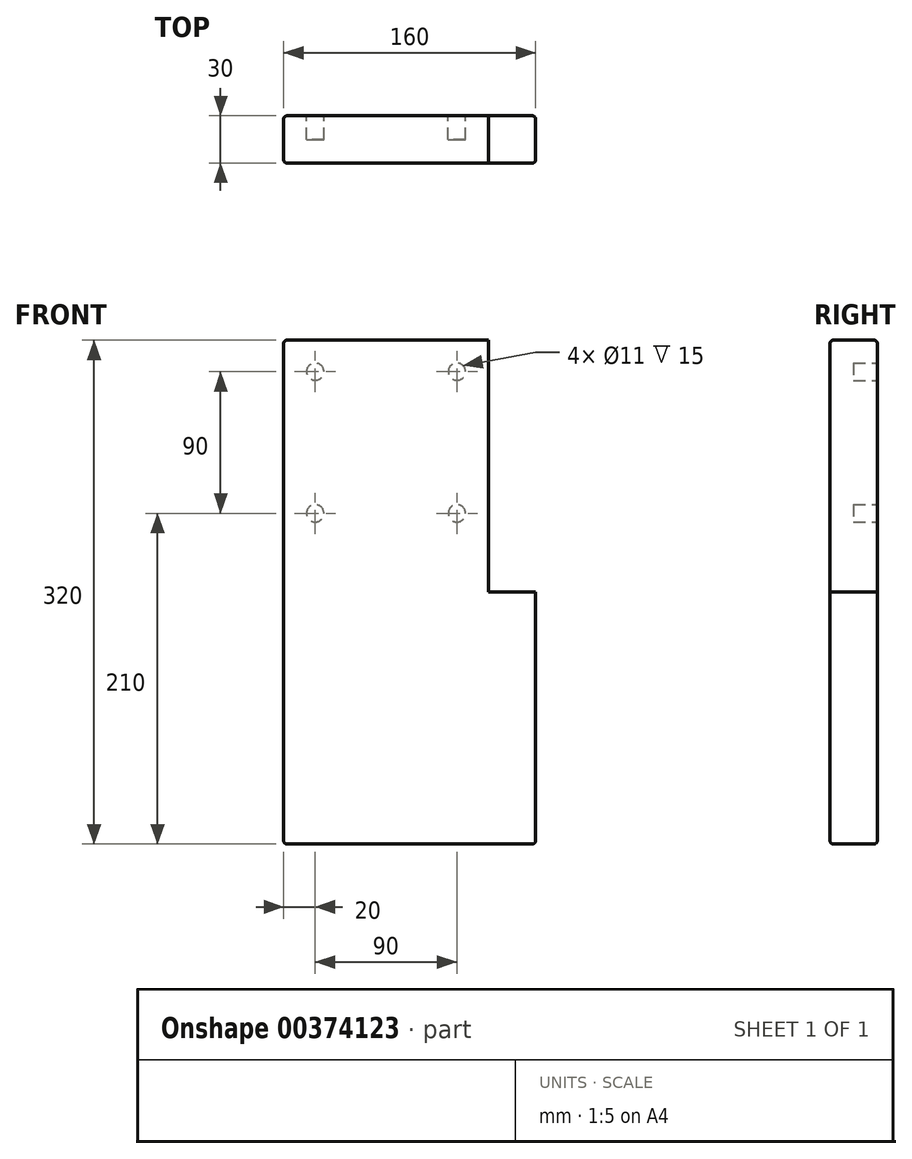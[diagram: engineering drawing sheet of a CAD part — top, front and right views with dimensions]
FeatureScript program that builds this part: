
annotation { "Feature Type Name" : "Feature", "Feature Type Description" : "" }
export const myFeature = defineFeature(function(context is Context, id is Id, definition is map)
    precondition{}
    {
        {
            var Q0;
            Q0=qCreatedBy(makeId("Top.planeOp"),FACE);
            var sketch = newSketch(context, id + "F0", { "sketchPlane" : qUnion([Q0])});
            skLineSegment(sketch, "E0.bottom", {"start": v(80, -15) * mm, "end": v(-80, -15) * mm});
            skLineSegment(sketch, "E0.top", {"start": v(80, 15) * mm, "end": v(-80, 15) * mm});
            skLineSegment(sketch, "E0.left", {"start": v(80, -15) * mm, "end": v(80, 15) * mm});
            skLineSegment(sketch, "E0.right", {"start": v(-80, -15) * mm, "end": v(-80, 15) * mm});
            skPoint(sketch, "E0.middle", {"position": v(0, 0) * mm});
            skSolve(sketch);
        }
        {
            var Q0;
            Q0 = qSketchRegion(id + "F0", true);
            extrude(context, id + "F1", {"entities" : qUnion([Q0]), "depth" : 320 * mm, "symmetric" : true});
        }
        {
            var Q0;
            Q0=makeQuery(id+"F1.opExtrude","SWEPT_FACE",FACE,{"disambiguationData":[OSD([sQuery(id+"F0.wireOp",EDGE,"E0.bottom")])]});
            var Q1;
            Q1=makeQuery(id+"F1.opExtrude","SWEPT_FACE",FACE,{"disambiguationData":[OSD([sQuery(id+"F0.wireOp",EDGE,"E0.top")])]});
            var Q2;
            Q2=makeQuery(id+"F1.opExtrude","CAP_FACE",FACE,{"disambiguationData":[OSD([sQuery(id+"F0.wireOp",EDGE,"E0.bottom"),sQuery(id+"F0.wireOp",EDGE,"E0.top"),sQuery(id+"F0.wireOp",EDGE,"E0.left"),sQuery(id+"F0.wireOp",EDGE,"E0.right")])],"isStart":false});
            var Q3;
            Q3=makeQuery(id+"F1.opExtrude","SWEPT_FACE",FACE,{"disambiguationData":[OSD([sQuery(id+"F0.wireOp",EDGE,"E0.left")])]});
            var Q4;
            Q4=makeQuery(id+"F1.opExtrude","SWEPT_FACE",FACE,{"disambiguationData":[OSD([sQuery(id+"F0.wireOp",EDGE,"E0.right")])]});
            var Q5;
            Q5=makeQuery(id+"F1.opExtrude","CAP_FACE",FACE,{"disambiguationData":[OSD([sQuery(id+"F0.wireOp",EDGE,"E0.bottom"),sQuery(id+"F0.wireOp",EDGE,"E0.top"),sQuery(id+"F0.wireOp",EDGE,"E0.left"),sQuery(id+"F0.wireOp",EDGE,"E0.right")])],"isStart":true});
            fillet(context, id + "F2", {"entities" : qUnion([Q0, Q1, Q2, Q3, Q4, Q5]), "radius" : 2 * mm, "tangentPropagation" : true, "allowEdgeOverflow" : false});
        }
        {
            var Q0;
            Q0=makeQuery(id+"F1.opExtrude","SWEPT_FACE",FACE,{"disambiguationData":[OSD([sQuery(id+"F0.wireOp",EDGE,"E0.top")])]});
            var sketch = newSketch(context, id + "F3", { "sketchPlane" : qUnion([Q0])});
            skLineSegment(sketch, "E1.bottom", {"start": v(-50, 0) * mm, "end": v(-80, 0) * mm});
            skLineSegment(sketch, "E1.top", {"start": v(-50, 160) * mm, "end": v(-80, 160) * mm});
            skLineSegment(sketch, "E1.left", {"start": v(-50, 0) * mm, "end": v(-50, 160) * mm});
            skLineSegment(sketch, "E1.right", {"start": v(-80, 0) * mm, "end": v(-80, 160) * mm});
            skCircle(sketch, "E2", {"center": v(60, 140) * mm, "radius": 5.5 * mm});
            skCircle(sketch, "E3.0.1.0", {"center": v(60, 50) * mm, "radius": 5.5 * mm});
            skCircle(sketch, "E3.1.0.0", {"center": v(-30, 140) * mm, "radius": 5.5 * mm});
            skCircle(sketch, "E3.1.1.0", {"center": v(-30, 50) * mm, "radius": 5.5 * mm});
            skLineSegment(sketch, "E3.direction1", {"start": v(60, 140) * mm, "end": v(-30, 140) * mm, "construction": true});
            skLineSegment(sketch, "E3.direction2", {"start": v(60, 140) * mm, "end": v(60, 50) * mm, "construction": true});
            skSolve(sketch);
        }
        {
            var Q0;
            {var subQ0=sQuery(id+"F3.wireOp",EDGE,"E1.left");var subQ1=sQuery(id+"F3.wireOp",EDGE,"E1.bottom");var subQ2=makeQuery(id+"F3.imprint","INTERSECT",VERTEX,{"derivedFrom":[subQ1,subQ0]});Q0=makeQuery(id+"F3.imprint","IMPRINT",FACE,{"disambiguationData":[TD([[makeQuery(id+"F3.imprint","IMPRINT",EDGE,{"disambiguationData":[TD([[subQ2,-1.0]])],"derivedFrom":subQ0}),1.0]])]});}
            var Q1;
            {var subQ2=sQuery(id+"F3.wireOp",EDGE,"E1.top");Q1=makeQuery(id+"F3.imprint","IMPRINT",FACE,{"disambiguationData":[TD([[makeQuery(id+"F3.imprint","IMPRINT",EDGE,{"derivedFrom":subQ2}),1.0]])]});}
            extrude(context, id + "F4", {"entities" : qUnion([Q0, Q1]), "operationType" : NewBodyOperationType.REMOVE, "endBound" : BoundingType.THROUGH_ALL, "oppositeDirection" : true, "depth" : 25 * mm});
        }
        {
            var Q0;
            Q0=makeQuery(id+"F3.imprint","IMPRINT",FACE,{"disambiguationData":[TD([[makeQuery(id+"F3.imprint","IMPRINT",EDGE,{"derivedFrom":sQuery(id+"F3.wireOp",EDGE,"E2")}),1.0]])]});
            var Q1;
            Q1=makeQuery(id+"F3.imprint","IMPRINT",FACE,{"disambiguationData":[TD([[makeQuery(id+"F3.imprint","IMPRINT",EDGE,{"derivedFrom":sQuery(id+"F3.wireOp",EDGE,"E3.1.0.0")}),1.0]])]});
            var Q2;
            Q2=makeQuery(id+"F3.imprint","IMPRINT",FACE,{"disambiguationData":[TD([[makeQuery(id+"F3.imprint","IMPRINT",EDGE,{"derivedFrom":sQuery(id+"F3.wireOp",EDGE,"E3.1.1.0")}),1.0]])]});
            var Q3;
            Q3=makeQuery(id+"F3.imprint","IMPRINT",FACE,{"disambiguationData":[TD([[makeQuery(id+"F3.imprint","IMPRINT",EDGE,{"derivedFrom":sQuery(id+"F3.wireOp",EDGE,"E3.0.1.0")}),1.0]])]});
            extrude(context, id + "F5", {"entities" : qUnion([Q0, Q1, Q2, Q3]), "operationType" : NewBodyOperationType.REMOVE, "oppositeDirection" : true, "depth" : 15 * mm});
        }
    });
